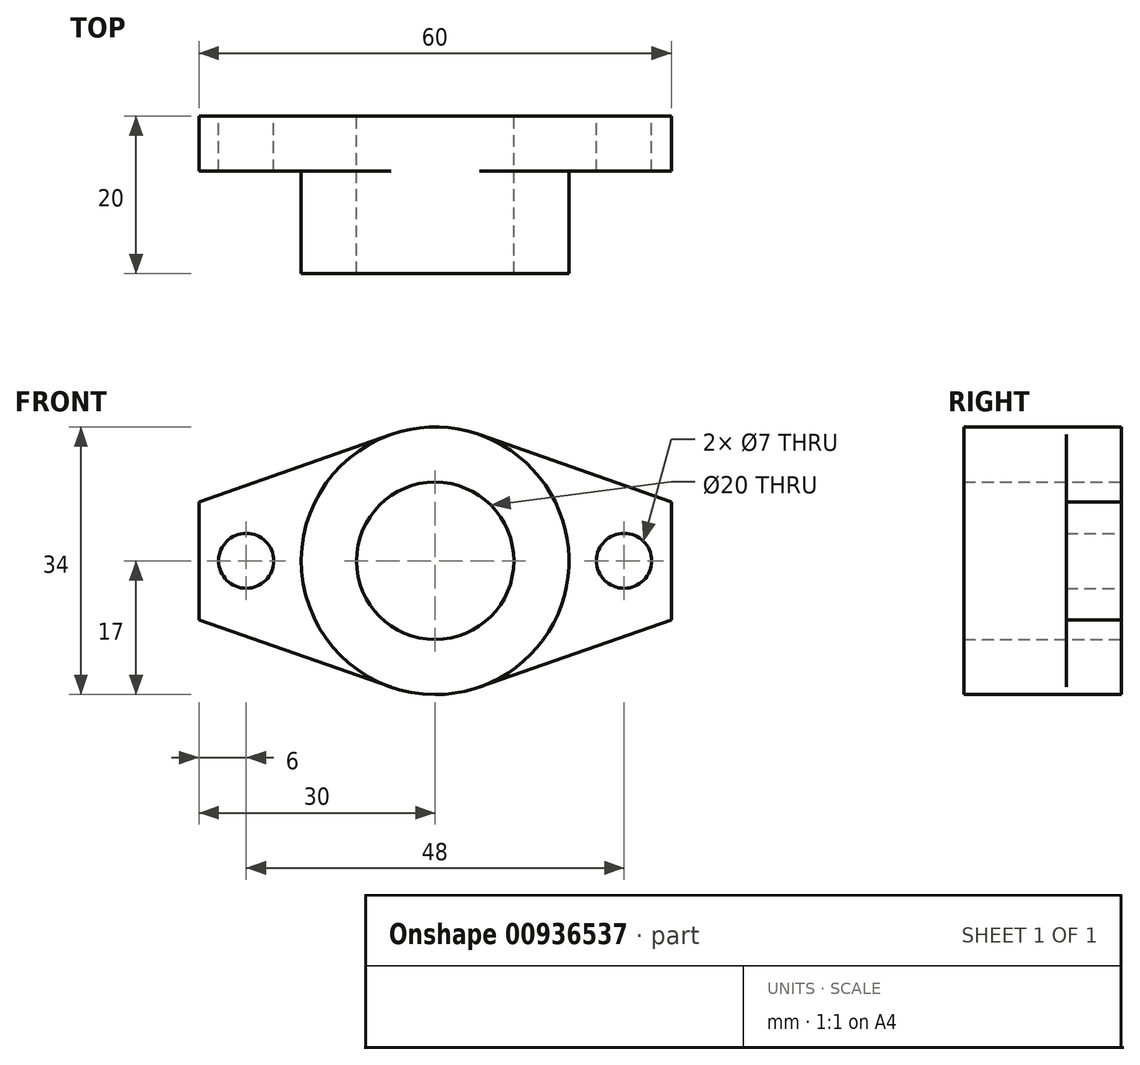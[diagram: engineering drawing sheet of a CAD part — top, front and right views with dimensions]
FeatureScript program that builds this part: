
annotation { "Feature Type Name" : "Feature", "Feature Type Description" : "" }
export const myFeature = defineFeature(function(context is Context, id is Id, definition is map)
    precondition{}
    {
        {
            var Q0;
            Q0=qCreatedBy(makeId("Front.planeOp"),FACE);
            var sketch = newSketch(context, id + "F0", { "sketchPlane" : qUnion([Q0])});
            skLineSegment(sketch, "E0", {"start": v(-78.22, 0) * mm, "end": v(83.48, 0) * mm, "construction": true});
            skLineSegment(sketch, "E1", {"start": v(-24, 6.55) * mm, "end": v(-24, -6.72) * mm, "construction": true});
            skLineSegment(sketch, "E2.MirrorCS", {"start": v(24, 6.55) * mm, "end": v(24, -6.72) * mm, "construction": true});
            skLineSegment(sketch, "E3.left", {"start": v(30, 7.5) * mm, "end": v(30, -7.5) * mm});
            skLineSegment(sketch, "E3.right", {"start": v(-30, 7.5) * mm, "end": v(-30, -7.5) * mm});
            skPoint(sketch, "E3.middle", {"position": v(0, 0) * mm});
            skCircle(sketch, "E4", {"center": v(-24, 0) * mm, "radius": 3.5 * mm});
            skCircle(sketch, "E5", {"center": v(24, 0) * mm, "radius": 3.5 * mm});
            skLineSegment(sketch, "E6", {"start": v(-30, 7.5) * mm, "end": v(-5.62, 16.04) * mm});
            skLineSegment(sketch, "E7.MirrorCS", {"start": v(30, 7.5) * mm, "end": v(5.62, 16.04) * mm});
            skLineSegment(sketch, "E8.MirrorCS", {"start": v(30, -7.5) * mm, "end": v(5.62, -16.04) * mm});
            skLineSegment(sketch, "E9.MirrorCS", {"start": v(-30, -7.5) * mm, "end": v(-5.62, -16.04) * mm});
            skArc(sketch, "E10.trimOffspring", {"start": v(5.62, 16.04) * mm, "mid": v(0, 17) * mm, "end": v(-5.62, 16.04) * mm});
            skArc(sketch, "E11.trimOffspring", {"start": v(-5.62, -16.04) * mm, "mid": v(0, -17) * mm, "end": v(5.62, -16.04) * mm});
            skCircle(sketch, "E12", {"center": v(0, 0) * mm, "radius": 10 * mm});
            skSolve(sketch);
        }
        {
            var Q0;
            Q0=makeQuery(id+"F0.imprint","IMPRINT",FACE,{"disambiguationData":[TD([[makeQuery(id+"F0.imprint","IMPRINT",EDGE,{"derivedFrom":sQuery(id+"F0.wireOp",EDGE,"E3.left")}),-1.0]])]});
            extrude(context, id + "F1", {"entities" : qUnion([Q0]), "depth" : 20 * mm, "offsetDistance" : 25 * mm});
        }
        {
            var Q0;
            Q0=makeQuery(id+"F1.opExtrude","CAP_FACE",FACE,{"disambiguationData":[OSD([sQuery(id+"F0.wireOp",EDGE,"E3.left"),sQuery(id+"F0.wireOp",EDGE,"E3.right"),sQuery(id+"F0.wireOp",EDGE,"E4"),sQuery(id+"F0.wireOp",EDGE,"E5"),sQuery(id+"F0.wireOp",EDGE,"E6"),sQuery(id+"F0.wireOp",EDGE,"E7.MirrorCS"),sQuery(id+"F0.wireOp",EDGE,"E8.MirrorCS"),sQuery(id+"F0.wireOp",EDGE,"E9.MirrorCS"),sQuery(id+"F0.wireOp",EDGE,"E10.trimOffspring"),sQuery(id+"F0.wireOp",EDGE,"E11.trimOffspring"),sQuery(id+"F0.wireOp",EDGE,"E12")])],"isStart":false});
            var sketch = newSketch(context, id + "F2", { "sketchPlane" : qUnion([Q0])});
            skLineSegment(sketch, "E13.0.0", {"start": v(-5.62, 16.04) * mm, "end": v(-30, 7.5) * mm});
            skLineSegment(sketch, "E13.0.2", {"start": v(-30, 7.5) * mm, "end": v(-5.62, 16.04) * mm});
            skLineSegment(sketch, "E14.0.0", {"start": v(-30, 7.5) * mm, "end": v(-30, -7.5) * mm});
            skLineSegment(sketch, "E14.0.2", {"start": v(-30, -7.5) * mm, "end": v(-30, 7.5) * mm});
            skLineSegment(sketch, "E15.0.0", {"start": v(-30, -7.5) * mm, "end": v(-5.62, -16.04) * mm});
            skLineSegment(sketch, "E15.0.2", {"start": v(-5.62, -16.04) * mm, "end": v(-30, -7.5) * mm});
            skLineSegment(sketch, "E16.0.0", {"start": v(5.62, -16.04) * mm, "end": v(30, -7.5) * mm});
            skLineSegment(sketch, "E16.0.2", {"start": v(30, -7.5) * mm, "end": v(5.62, -16.04) * mm});
            skLineSegment(sketch, "E17.0.0", {"start": v(30, -7.5) * mm, "end": v(30, 7.5) * mm});
            skLineSegment(sketch, "E17.0.2", {"start": v(30, 7.5) * mm, "end": v(30, -7.5) * mm});
            skLineSegment(sketch, "E18.0.0", {"start": v(30, 7.5) * mm, "end": v(5.62, 16.04) * mm});
            skLineSegment(sketch, "E18.0.2", {"start": v(5.62, 16.04) * mm, "end": v(30, 7.5) * mm});
            skArc(sketch, "E19", {"start": v(-5.62, 16.04) * mm, "mid": v(-17, 0) * mm, "end": v(-5.62, -16.04) * mm});
            skArc(sketch, "E20", {"start": v(5.62, 16.04) * mm, "mid": v(17, 0) * mm, "end": v(5.62, -16.04) * mm});
            skSolve(sketch);
        }
        {
            var Q0;
            Q0=qSketchRegion(id+"F2",true);
            extrude(context, id + "F3", {"entities" : qUnion([Q0]), "operationType" : NewBodyOperationType.REMOVE, "oppositeDirection" : true, "depth" : 13 * mm, "offsetDistance" : 25 * mm});
        }
    });
